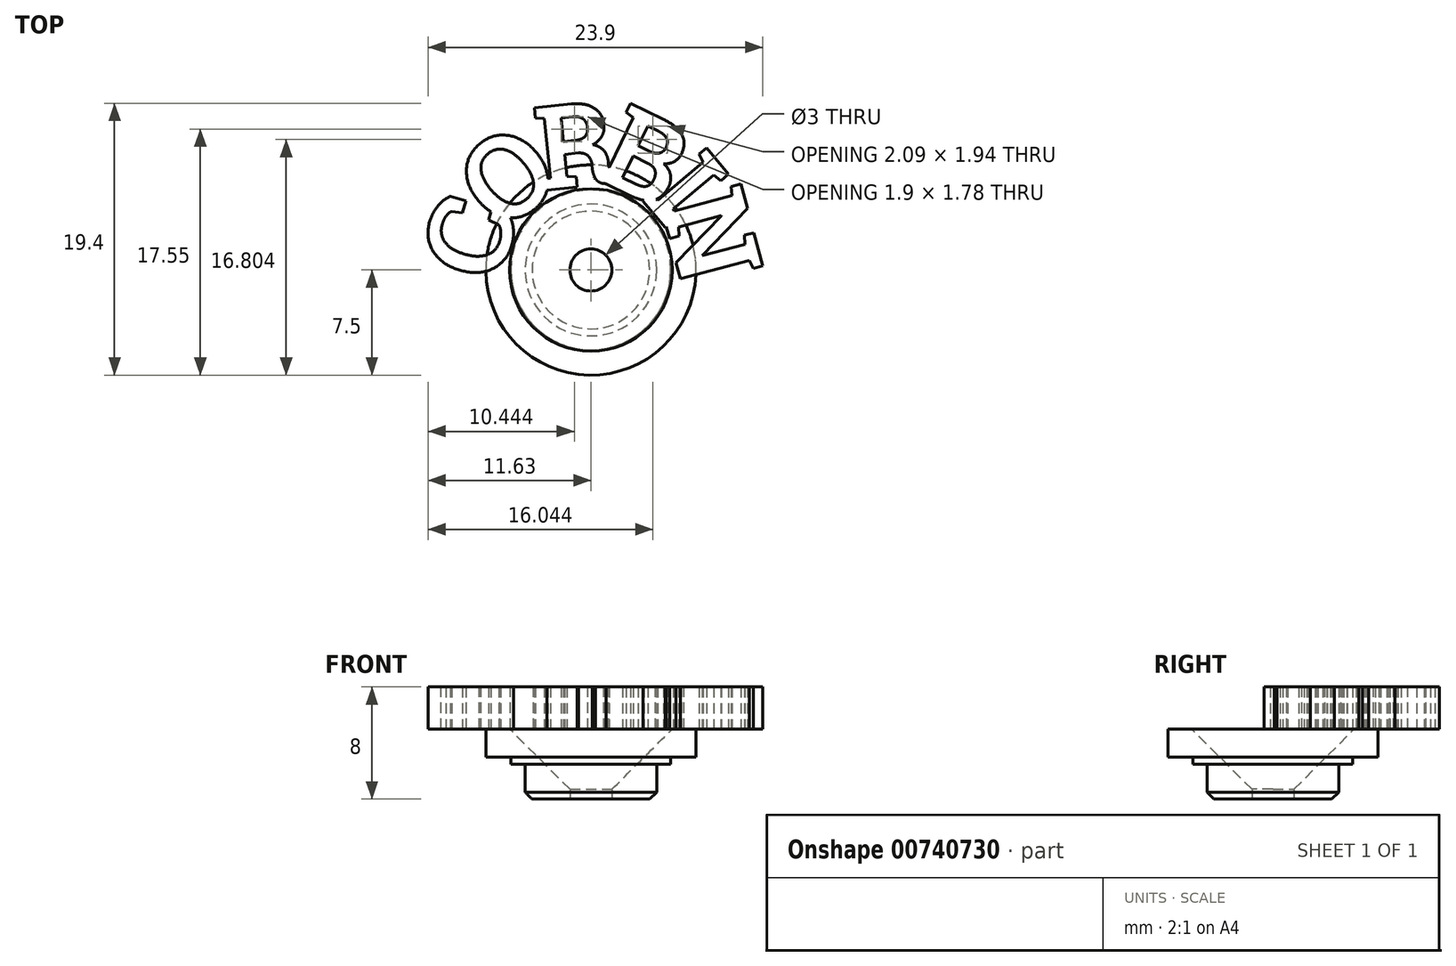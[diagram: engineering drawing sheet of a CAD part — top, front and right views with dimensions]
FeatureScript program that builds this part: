
annotation { "Feature Type Name" : "Feature", "Feature Type Description" : "" }
export const myFeature = defineFeature(function(context is Context, id is Id, definition is map)
    precondition{}
    {
        {
            var Q0;
            Q0=qCreatedBy(makeId("Top.planeOp"),FACE);
            var sketch = newSketch(context, id + "F0", { "sketchPlane" : qUnion([Q0])});
            skCircle(sketch, "E0", {"center": v(0, 0) * mm, "radius": 7.5 * mm});
            skLineSegment(sketch, "E1", {"start": v(0, 19.33) * mm, "end": v(0, -22.56) * mm, "construction": true});
            skLineSegment(sketch, "E2", {"start": v(17.52, 0) * mm, "end": v(-21.05, 0) * mm, "construction": true});
            skSolve(sketch);
        }
        {
            var Q0;
            Q0=qSketchRegion(id+"F0",true);
            extrude(context, id + "F1", {"entities" : qUnion([Q0]), "depth" : 2 * mm, "offsetDistance" : 25 * mm});
        }
        {
            var Q0;
            Q0=makeQuery(id+"F1.opExtrude","CAP_FACE",FACE,{"disambiguationData":[OSD([sQuery(id+"F0.wireOp",EDGE,"E0")])],"isStart":true});
            var sketch = newSketch(context, id + "F2", { "sketchPlane" : qUnion([Q0])});
            skCircle(sketch, "E3", {"center": v(0, 0) * mm, "radius": 4.7 * mm});
            skSolve(sketch);
        }
        {
            var Q0;
            Q0=qSketchRegion(id+"F2",true);
            extrude(context, id + "F3", {"entities" : qUnion([Q0]), "operationType" : NewBodyOperationType.ADD, "depth" : 3 * mm, "offsetDistance" : 25 * mm});
        }
        {
            var Q0;
            Q0=makeQuery(id+"F3.opExtrude","CAP_EDGE",EDGE,{"disambiguationData":[OSD([sQuery(id+"F2.wireOp",EDGE,"E3")])],"isStart":false});
            chamfer(context, id + "F4", {"entities" : qUnion([Q0]), "width" : .5 * mm, "tangentPropagation" : true});
        }
        {
            var Q0;
            Q0=makeQuery(id+"F3.opExtrude","CAP_FACE",FACE,{"disambiguationData":[OSD([sQuery(id+"F2.wireOp",EDGE,"E3")])],"isStart":false});
            var sketch = newSketch(context, id + "F5", { "sketchPlane" : qUnion([Q0])});
            skCircle(sketch, "E4", {"center": v(0, 0) * mm, "radius": 1.5 * mm});
            skSolve(sketch);
        }
        {
            var Q0;
            Q0=qSketchRegion(id+"F5",true);
            extrude(context, id + "F6", {"entities" : qUnion([Q0]), "operationType" : NewBodyOperationType.REMOVE, "oppositeDirection" : true, "depth" : 25 * mm, "offsetDistance" : 25 * mm});
        }
        {
            var Q0;
            Q0=makeQuery(id+"F1.opExtrude","CAP_FACE",FACE,{"disambiguationData":[OSD([sQuery(id+"F0.wireOp",EDGE,"E0")])],"isStart":true});
            var sketch = newSketch(context, id + "F7", { "sketchPlane" : qUnion([Q0])});
            skCircle(sketch, "E5.0", {"center": v(0, 0) * mm, "radius": 5.7 * mm});
            skCircle(sketch, "E6.0", {"center": v(0, 0) * mm, "radius": 4.7 * mm});
            skSolve(sketch);
        }
        {
            var Q0;
            Q0=qSketchRegion(id+"F7",true);
            extrude(context, id + "F8", {"entities" : qUnion([Q0]), "operationType" : NewBodyOperationType.ADD, "depth" : .5 * mm, "offsetDistance" : 25 * mm});
        }
        {
            var Q0;
            Q0=makeQuery(id+"F1.opExtrude","CAP_FACE",FACE,{"disambiguationData":[OSD([sQuery(id+"F0.wireOp",EDGE,"E0")])],"isStart":false});
            var sketch = newSketch(context, id + "F9", { "sketchPlane" : qUnion([Q0])});
            skText(sketch, "E7", { "text": "C", "fontName": "RobotoSlab-Bold.ttf"});
            skText(sketch, "E8", { "text": "O", "fontName": "RobotoSlab-Bold.ttf"});
            skText(sketch, "E9", { "text": "B", "fontName": "RobotoSlab-Bold.ttf"});
            skText(sketch, "E10", { "text": "R", "fontName": "RobotoSlab-Bold.ttf"});
            skLineSegment(sketch, "E11", {"start": v(0, 0) * mm, "end": v(-14.65, 4.2) * mm, "construction": true});
            skLineSegment(sketch, "E12", {"start": v(0, 0) * mm, "end": v(6.95, 14.26) * mm, "construction": true});
            skLineSegment(sketch, "E13", {"start": v(0, 0) * mm, "end": v(-1.78, 16.95) * mm, "construction": true});
            skLineSegment(sketch, "E14", {"start": v(0, 0) * mm, "end": v(-10.5, 12.08) * mm, "construction": true});
            skLineSegment(sketch, "E15", {"start": v(0, 0) * mm, "end": v(21.4, 0) * mm, "construction": true});
            skLineSegment(sketch, "E16", {"start": v(0, 0) * mm, "end": v(16.04, 13.46) * mm, "construction": true});
            skLineSegment(sketch, "E17", {"start": v(0, 0) * mm, "end": v(20.52, 5.5) * mm, "construction": true});
            skText(sketch, "E18", { "text": "I", "fontName": "RobotoSlab-Bold.ttf"});
            skText(sketch, "E19", { "text": "N", "fontName": "RobotoSlab-Bold.ttf"});
            const initialGuessF9  = {"E7": [-0.00654, -0.00103, 0.27564, 0.96126, 0.006], "E8": [-0.00626, 0.0025, 0.7547, 0.65606, 0.006], "E9": [2e-05, 0.00667, 0.8988, -0.43837, 0.006], "E10": [-0.00365, 0.00565, 0.99452, 0.10453, 0.006], "E18": [0.00357, 0.00508, 0.64279, -0.76604, 0.006], "E19": [0.00492, 0.00483, 0.25882, -0.96593, 0.006]};
            skSetInitialGuess(sketch, initialGuessF9);
            skSolve(sketch);
        }
        {
            var Q0;
            Q0=qSketchRegion(id+"F9",true);
            extrude(context, id + "F10", {"entities" : qUnion([Q0]), "operationType" : NewBodyOperationType.ADD, "depth" : 3 * mm, "offsetDistance" : 25 * mm});
        }
        {
            var Q0;
            Q0=makeQuery(id+"F6.boolean.opBoolean","INTERSECT",EDGE,{"derivedFrom":[makeQuery(id+"F1.opExtrude","CAP_FACE",FACE,{"disambiguationData":[OSD([sQuery(id+"F0.wireOp",EDGE,"E0")])],"isStart":false}),makeQuery(id+"F6.opExtrude","SWEPT_FACE",FACE,{"disambiguationData":[OSD([sQuery(id+"F5.wireOp",EDGE,"E4")])]})]});
            chamfer(context, id + "F11", {"entities" : qUnion([Q0]), "width" : 4.3 * mm, "tangentPropagation" : true});
        }
    });
